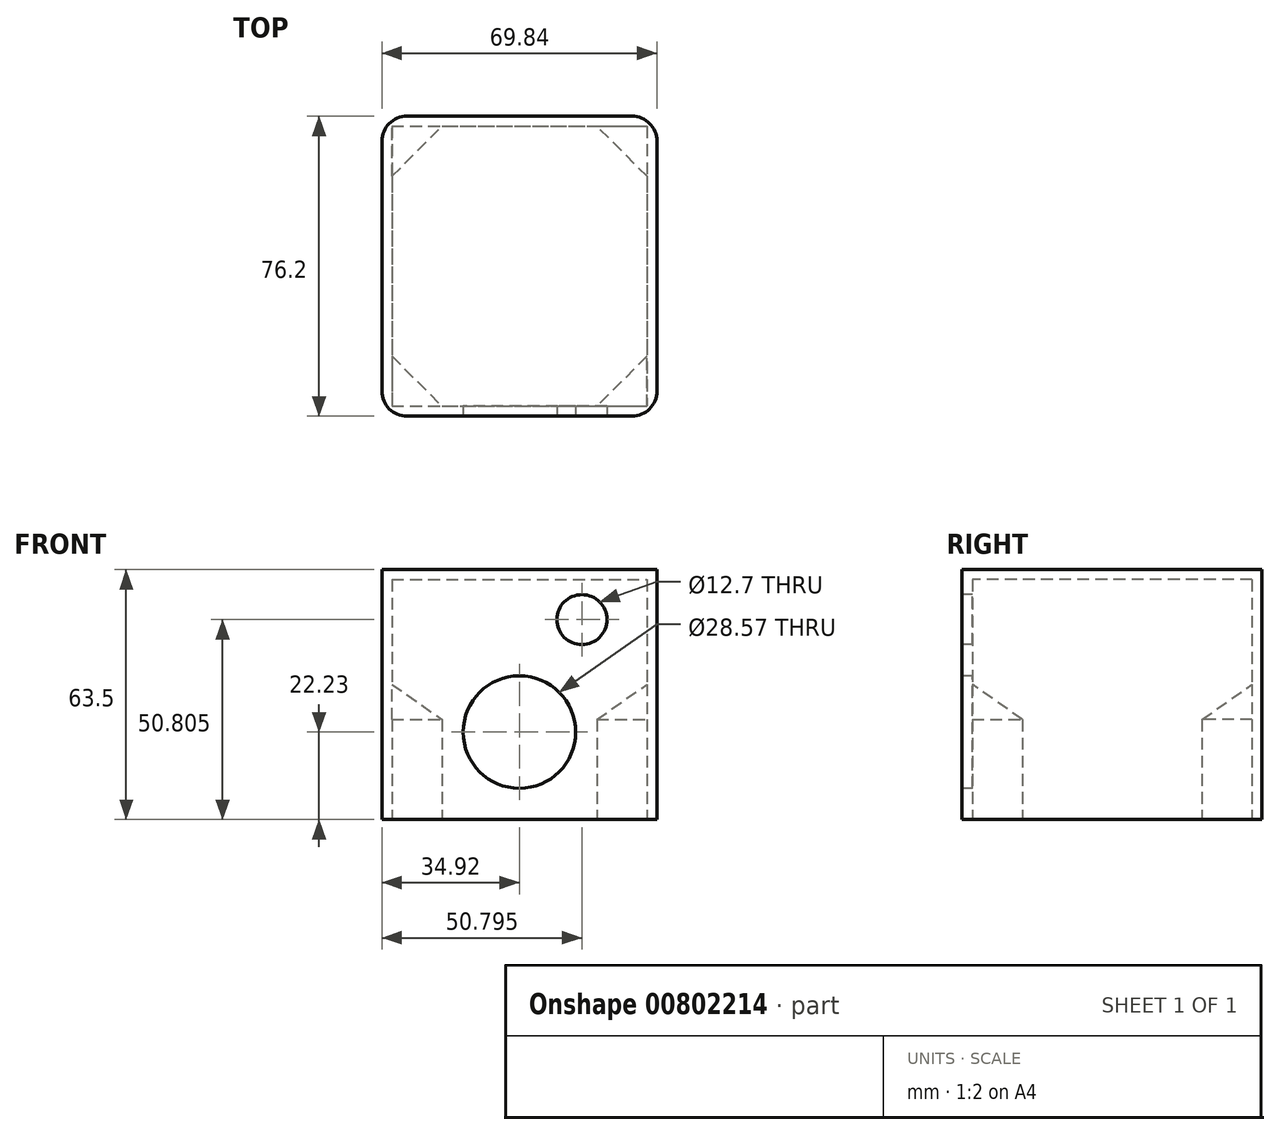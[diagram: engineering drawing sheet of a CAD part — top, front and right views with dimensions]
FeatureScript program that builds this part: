
annotation { "Feature Type Name" : "Feature", "Feature Type Description" : "" }
export const myFeature = defineFeature(function(context is Context, id is Id, definition is map)
    precondition{}
    {
        {
            var Q0;
            Q0=qCreatedBy(makeId("Front.planeOp"),FACE);
            var sketch = newSketch(context, id + "F0", { "sketchPlane" : qUnion([Q0])});
            skCircle(sketch, "E0", {"center": v(0, 0) * mm, "radius": 14.29 * mm, "construction": true});
            skCircle(sketch, "E1", {"center": v(0, 0) * mm, "radius": 19.05 * mm, "construction": true});
            skLineSegment(sketch, "E2.bottom", {"start": v(-34.93, 41.28) * mm, "end": v(34.93, 41.28) * mm});
            skLineSegment(sketch, "E2.top", {"start": v(-34.93, -22.22) * mm, "end": v(34.92, -22.22) * mm});
            skLineSegment(sketch, "E2.left", {"start": v(-34.93, 41.28) * mm, "end": v(-34.93, -22.22) * mm});
            skLineSegment(sketch, "E2.right", {"start": v(34.93, 41.28) * mm, "end": v(34.93, -22.22) * mm});
            skSolve(sketch);
        }
        {
            var Q0;
            Q0=makeQuery(id+"F0.imprint","IMPRINT",FACE,{"disambiguationData":[TD([[makeQuery(id+"F0.imprint","IMPRINT",EDGE,{"derivedFrom":sQuery(id+"F0.wireOp",EDGE,"E2.bottom")}),-1.0]])]});
            var Q1;
            Q1=sQuery(id+"F0.wireOp",EDGE,"E0");
            extrude(context, id + "F1", {"entities" : qUnion([Q0]), "surfaceEntities" : qUnion([Q1]), "oppositeDirection" : true, "depth" : 76.2 * mm, "offsetDistance" : 25.4 * mm});
        }
        {
            var Q0;
            Q0=makeQuery(id+"F1.opExtrude","SWEPT_FACE",FACE,{"disambiguationData":[OSD([sQuery(id+"F0.wireOp",EDGE,"E2.top")])]});
            shell(context, id + "F2", {"entities" : qUnion([Q0]), "thickness" : 2.54 * mm});
        }
        {
            var Q0;
            Q0=makeQuery(id+"F1.opExtrude","CAP_FACE",FACE,{"disambiguationData":[OSD([sQuery(id+"F0.wireOp",EDGE,"E2.bottom"),sQuery(id+"F0.wireOp",EDGE,"E2.top"),sQuery(id+"F0.wireOp",EDGE,"E2.left"),sQuery(id+"F0.wireOp",EDGE,"E2.right")])],"isStart":true});
            var sketch = newSketch(context, id + "F3", { "sketchPlane" : qUnion([Q0])});
            skCircle(sketch, "E3", {"center": v(0, 0) * mm, "radius": 14.29 * mm});
            skCircle(sketch, "E4", {"center": v(15.87, 28.57) * mm, "radius": 6.35 * mm});
            skSolve(sketch);
        }
        {
            var Q0;
            Q0 = qSketchRegion(id + "F3", true);
            extrude(context, id + "F4", {"entities" : qUnion([Q0]), "operationType" : NewBodyOperationType.REMOVE, "endBound" : BoundingType.UP_TO_NEXT, "oppositeDirection" : true, "depth" : 25.4 * mm, "offsetDistance" : 25.4 * mm});
        }
        {
            var Q0;
            Q0=makeQuery(id+"F1.opExtrude","CAP_EDGE",EDGE,{"disambiguationData":[OSD([sQuery(id+"F0.wireOp",EDGE,"E2.left")])],"isStart":true});
            var Q1;
            Q1=makeQuery(id+"F1.opExtrude","CAP_EDGE",EDGE,{"disambiguationData":[OSD([sQuery(id+"F0.wireOp",EDGE,"E2.right")])],"isStart":true});
            var Q2;
            Q2=makeQuery(id+"F1.opExtrude","CAP_EDGE",EDGE,{"disambiguationData":[OSD([sQuery(id+"F0.wireOp",EDGE,"E2.left")])],"isStart":false});
            var Q3;
            Q3=makeQuery(id+"F1.opExtrude","CAP_EDGE",EDGE,{"disambiguationData":[OSD([sQuery(id+"F0.wireOp",EDGE,"E2.right")])],"isStart":false});
            fillet(context, id + "F5", {"entities" : qUnion([Q0, Q1, Q2, Q3]), "radius" : 6.35 * mm, "tangentPropagation" : true, "allowEdgeOverflow" : false});
        }
        {
            var Q0;
            Q0=makeQuery(id+"F1.opExtrude","SWEPT_FACE",FACE,{"disambiguationData":[OSD([sQuery(id+"F0.wireOp",EDGE,"E2.top")])]});
            var sketch = newSketch(context, id + "F6", { "sketchPlane" : qUnion([Q0])});
            skLineSegment(sketch, "E5", {"start": v(19.69, -2.54) * mm, "end": v(32.39, -2.54) * mm});
            skLineSegment(sketch, "E6", {"start": v(32.39, -2.54) * mm, "end": v(32.39, -15.24) * mm});
            skLineSegment(sketch, "E7", {"start": v(32.39, -15.24) * mm, "end": v(19.69, -2.54) * mm});
            skSolve(sketch);
        }
        {
            var Q0;
            Q0=makeQuery(id+"F6.imprint","IMPRINT",FACE,{"disambiguationData":[TD([[makeQuery(id+"F6.imprint","IMPRINT",EDGE,{"derivedFrom":sQuery(id+"F6.wireOp",EDGE,"E5")}),-1.0]])]});
            extrude(context, id + "F7", {"entities" : qUnion([Q0]), "oppositeDirection" : true, "depth" : 38.1 * mm, "offsetDistance" : 25.4 * mm});
        }
        {
            var Q0;
            Q0=makeQuery(id+"F7.opExtrude","SWEPT_BODY",BODY,{"disambiguationData":[OSD([sQuery(id+"F6.wireOp",EDGE,"E5"),sQuery(id+"F6.wireOp",EDGE,"E6"),sQuery(id+"F6.wireOp",EDGE,"E7")])]});
            var Q1;
            Q1=qCreatedBy(makeId("Right.planeOp"),FACE);
            mirror(context, id + "F8", {"entities" : qUnion([Q0]), "mirrorPlane" : qUnion([Q1])});
        }
        {
            var Q0;
            Q0=makeQuery(id+"F8.opPattern","COPY",EDGE,{"derivedFrom":makeQuery(id+"F7.opExtrude","CAP_EDGE",EDGE,{"disambiguationData":[OSD([sQuery(id+"F6.wireOp",EDGE,"E7")])],"isStart":false}),"instanceName":"1"});
            var Q1;
            Q1=makeQuery(id+"F7.opExtrude","CAP_EDGE",EDGE,{"disambiguationData":[OSD([sQuery(id+"F6.wireOp",EDGE,"E7")])],"isStart":false});
            chamfer(context, id + "F9", {"entities" : qUnion([Q0, Q1]), "width" : 12.7 * mm, "tangentPropagation" : true});
        }
        {
            var Q0;
            Q0=makeQuery(id+"F1.opExtrude","CAP_FACE",FACE,{"disambiguationData":[OSD([sQuery(id+"F0.wireOp",EDGE,"E2.bottom"),sQuery(id+"F0.wireOp",EDGE,"E2.top"),sQuery(id+"F0.wireOp",EDGE,"E2.left"),sQuery(id+"F0.wireOp",EDGE,"E2.right")])],"isStart":false});
            cPlane(context, id + "F10", {"entities" : qUnion([Q0]), "cplaneType" : CPlaneType.OFFSET, "offset" : 38.1 * mm, "oppositeDirection" : true, "width" : 152.4 * mm, "height" : 152.4 * mm});
        }
        {
            var Q0;
            Q0=makeQuery(id+"F8.opPattern","COPY",BODY,{"derivedFrom":makeQuery(id+"F7.opExtrude","SWEPT_BODY",BODY,{"disambiguationData":[OSD([sQuery(id+"F6.wireOp",EDGE,"E5"),sQuery(id+"F6.wireOp",EDGE,"E6"),sQuery(id+"F6.wireOp",EDGE,"E7")])]}),"instanceName":"1"});
            var Q1;
            Q1=makeQuery(id+"F7.opExtrude","SWEPT_BODY",BODY,{"disambiguationData":[OSD([sQuery(id+"F6.wireOp",EDGE,"E5"),sQuery(id+"F6.wireOp",EDGE,"E6"),sQuery(id+"F6.wireOp",EDGE,"E7")])]});
            var Q2;
            Q2=qCreatedBy(id+"F10.planeOp",FACE);
            mirror(context, id + "F11", {"operationType" : NewBodyOperationType.ADD, "entities" : qUnion([Q0, Q1]), "mirrorPlane" : qUnion([Q2])});
        }
    });
